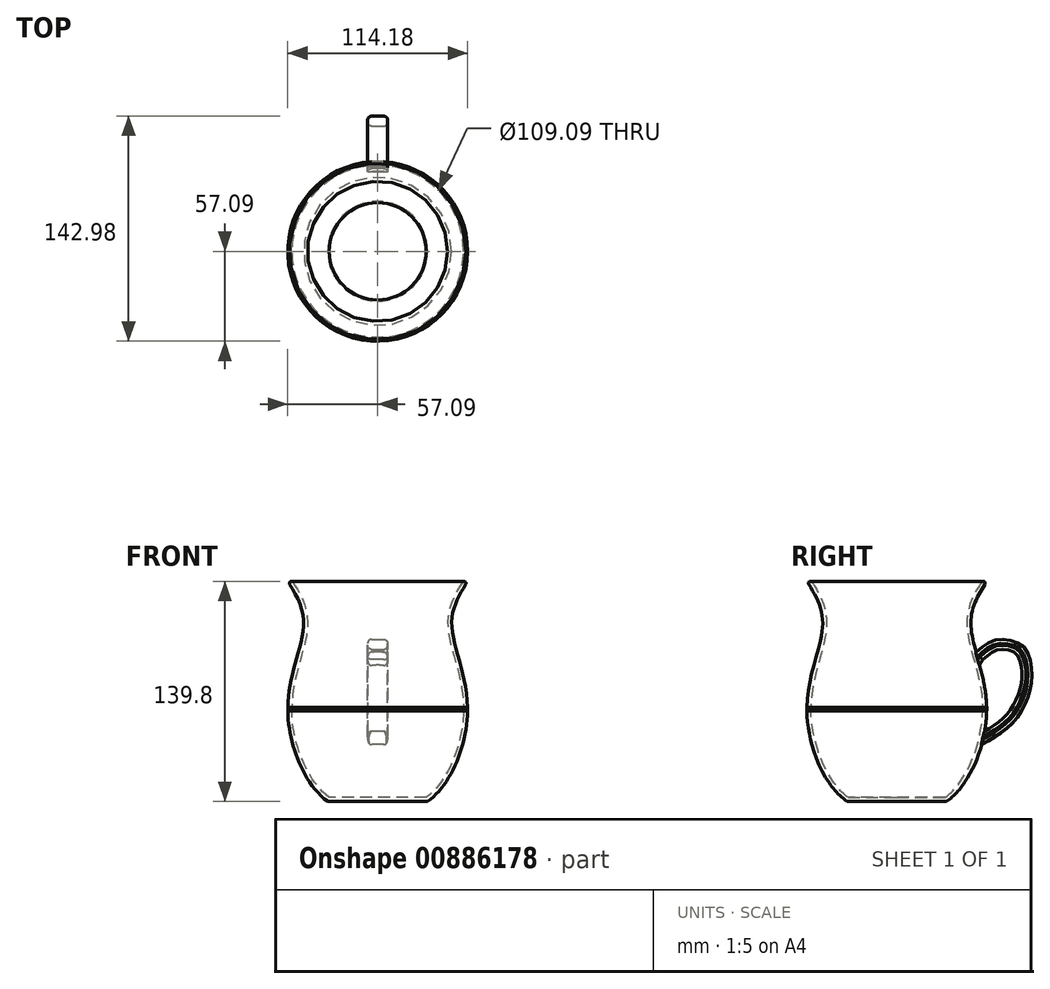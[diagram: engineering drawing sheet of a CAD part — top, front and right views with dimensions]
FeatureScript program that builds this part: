
annotation { "Feature Type Name" : "Feature", "Feature Type Description" : "" }
export const myFeature = defineFeature(function(context is Context, id is Id, definition is map)
    precondition{}
    {
        {
            var Q0;
            Q0=qCreatedBy(makeId("Front.planeOp"),FACE);
            var sketch = newSketch(context, id + "F0", { "sketchPlane" : qUnion([Q0])});
            skLineSegment(sketch, "E0.bottom", {"start": v(0, -69.9) * mm, "end": v(31.65, -69.9) * mm});
            skLineSegment(sketch, "E0.top", {"start": v(0, 69.9) * mm, "end": v(57.09, 69.9) * mm});
            skLineSegment(sketch, "E0.right", {"start": v(57.09, -12.27) * mm, "end": v(57.09, -10.35) * mm});
            skPoint(sketch, "E0.middle", {"position": v(0, 0) * mm});
            skFitSpline(sketch, "E1", {"points": [v(57.09, 69.9) * mm, v(47.03, 43.48) * mm, v(57.09, -10.35) * mm, v(31.65, -69.9) * mm, v(-8.28, -73.95) * mm], "startDerivative": vector(-76.93, -123.75) * mm, "endDerivative": vector(-181.25, 25.51) * mm});
            skLineSegment(sketch, "E2", {"start": v(0, 69.9) * mm, "end": v(0, -69.9) * mm});
            skPoint(sketch, "E3.orphan", {"position": v(57.09, -69.9) * mm});
            skPoint(sketch, "E0.left.end.orphan", {"position": v(-57.09, 69.9) * mm});
            skPoint(sketch, "E4.orphan", {"position": v(-57.09, -69.9) * mm});
            skSolve(sketch);
        }
        {
            var Q0;
            {var subQ3=sQuery(id+"F0.wireOp",EDGE,"E0.bottom");Q0=makeQuery(id+"F0.imprint","IMPRINT",FACE,{"disambiguationData":[TD([[makeQuery(id+"F0.imprint","IMPRINT",EDGE,{"derivedFrom":subQ3}),1.0]])]});}
            var Q1;
            Q1=sQuery(id+"F0.wireOp",EDGE,"E0.top");
            var Q2;
            Q2=sQuery(id+"F0.wireOp",EDGE,"E1");
            var Q3;
            Q3=sQuery(id+"F0.wireOp",EDGE,"E2");
            var Q4;
            Q4=sQuery(id+"F0.wireOp",EDGE,"E0.bottom");
            var Q5;
            Q5=sQuery(id+"F0.wireOp",EDGE,"E2");
            revolve(context, id + "F1", {"surfaceOperationType" : NewSurfaceOperationType.NEW, "entities" : qUnion([Q0]), "surfaceEntities" : qUnion([Q1, Q2, Q3, Q4]), "axis" : qUnion([Q5]), "revolveType" : RevolveType.FULL});
        }
        {
            var Q0;
            Q0=makeQuery(id+"F1.opRevolve","SWEPT_FACE",FACE,{"disambiguationData":[OSD([sQuery(id+"F0.wireOp",EDGE,"E0.top")])]});
            shell(context, id + "F2", {"entities" : qUnion([Q0]), "thickness" : 2.54 * mm});
        }
        {
            var Q0;
            Q0=qCreatedBy(makeId("Right.planeOp"),FACE);
            var sketch = newSketch(context, id + "F3", { "sketchPlane" : qUnion([Q0])});
            skFitSpline(sketch, "E5", {"points": [v(50.58, 25.14) * mm, v(63.89, 32.83) * mm, v(79.27, 29.28) * mm, v(84.3, 21.3) * mm, v(85.78, 7.7) * mm, v(80.75, -9.76) * mm, v(70.99, -22.48) * mm, v(52.95, -34.31) * mm], "startDerivative": vector(85.65, 71.96) * mm, "endDerivative": vector(-116.74, -67.27) * mm});
            skFitSpline(sketch, "E6.0", {"points": [v(54.66, 20.28) * mm, v(55.56, 21.03) * mm, v(57.26, 22.46) * mm, v(59.64, 24.26) * mm, v(61.47, 25.36) * mm, v(62.84, 25.99) * mm, v(63.68, 26.28) * mm, v(64.34, 26.45) * mm, v(64.75, 26.54) * mm, v(65.1, 26.6) * mm, v(65.44, 26.64) * mm, v(65.9, 26.69) * mm, v(66.5, 26.72) * mm, v(67.32, 26.72) * mm, v(68.4, 26.64) * mm, v(69.73, 26.45) * mm, v(71.5, 26.05) * mm, v(73.16, 25.47) * mm, v(74.53, 24.8) * mm, v(75.35, 24.3) * mm, v(75.92, 23.85) * mm, v(76.36, 23.42) * mm, v(76.73, 22.98) * mm, v(77.06, 22.46) * mm, v(77.4, 21.81) * mm, v(77.72, 21) * mm, v(78, 20.2) * mm, v(78.22, 19.45) * mm, v(78.44, 18.68) * mm, v(78.7, 17.68) * mm, v(79.05, 16.03) * mm, v(79.39, 13.85) * mm, v(79.54, 11.56) * mm, v(79.54, 9.68) * mm, v(79.48, 8.48) * mm, v(79.39, 7.5) * mm, v(79.28, 6.52) * mm, v(79.09, 5.25) * mm, v(78.79, 3.69) * mm, v(78.3, 1.58) * mm, v(77.52, -1.06) * mm, v(76.36, -4.17) * mm, v(75.02, -7.1) * mm, v(73.58, -9.74) * mm, v(72, -12.13) * mm, v(70.25, -14.34) * mm, v(68.25, -16.44) * mm, v(65.95, -18.48) * mm, v(63.23, -20.53) * mm, v(60.2, -22.6) * mm, v(56.9, -24.65) * mm, v(53.4, -26.72) * mm, v(51, -28.1) * mm, v(49.78, -28.8) * mm]});
            skFitSpline(sketch, "E7", {"points": [v(54.66, 20.28) * mm, v(51.17, 12.72) * mm, v(51.76, 11.54) * mm], "startDerivative": vector(-7.37, -12.87) * mm, "endDerivative": vector(3.07, -3.24) * mm});
            skLineSegment(sketch, "E8", {"start": v(50.58, 25.14) * mm, "end": v(48.03, 22.78) * mm});
            skLineSegment(sketch, "E9", {"start": v(49.96, 24.57) * mm, "end": v(52.2, 15.8) * mm});
            skLineSegment(sketch, "E10", {"start": v(55.67, -25.37) * mm, "end": v(53.65, -33.9) * mm});
            skSolve(sketch);
        }
        {
            var Q0;
            {var subQ3=sQuery(id+"F3.wireOp",EDGE,"E9");Q0=makeQuery(id+"F3.imprint","IMPRINT",FACE,{"disambiguationData":[TD([[makeQuery(id+"F3.imprint","IMPRINT",EDGE,{"derivedFrom":subQ3}),1.0]])]});}
            extrude(context, id + "F4", {"entities" : qUnion([Q0]), "operationType" : NewBodyOperationType.ADD, "depth" : 6.35 * mm, "offsetDistance" : 25.4 * mm, "hasSecondDirection" : true, "secondDirectionOppositeDirection" : true, "secondDirectionDepth" : 6.35 * mm});
        }
        {
            var Q0;
            Q0=makeQuery(id+"F4.opExtrude","CAP_EDGE",EDGE,{"disambiguationData":[OSD([sQuery(id+"F3.wireOp",EDGE,"E5")])],"isStart":false});
            var Q1;
            Q1=makeQuery(id+"F4.opExtrude","CAP_EDGE",EDGE,{"disambiguationData":[OSD([sQuery(id+"F3.wireOp",EDGE,"E5")])],"isStart":true});
            var Q2;
            Q2=makeQuery(id+"F4.opExtrude","CAP_EDGE",EDGE,{"disambiguationData":[OSD([sQuery(id+"F3.wireOp",EDGE,"E6.0")])],"isStart":true});
            var Q3;
            Q3=makeQuery(id+"F4.opExtrude","CAP_EDGE",EDGE,{"disambiguationData":[OSD([sQuery(id+"F3.wireOp",EDGE,"E7")])],"isStart":true});
            var Q4;
            Q4=makeQuery(id+"F4.opExtrude","CAP_EDGE",EDGE,{"disambiguationData":[OSD([sQuery(id+"F3.wireOp",EDGE,"E6.0")])],"isStart":false});
            var Q5;
            Q5=makeQuery(id+"F4.opExtrude","CAP_EDGE",EDGE,{"disambiguationData":[OSD([sQuery(id+"F3.wireOp",EDGE,"E7")])],"isStart":false});
            fillet(context, id + "F5", {"entities" : qUnion([Q0, Q1, Q2, Q3, Q4, Q5]), "radius" : 2.54 * mm, "tangentPropagation" : true, "allowEdgeOverflow" : false});
        }
        {
            var Q0;
            Q0=makeQuery(id+"F2.opShell","OFFSET_EDGE",EDGE,{"disambiguationData":[OSD([sQuery(id+"F0.wireOp",EDGE,"E0.top"),sQuery(id+"F0.wireOp",EDGE,"E1")])]});
            var Q1;
            Q1=makeQuery(id+"F1.opRevolve","SWEPT_EDGE",EDGE,{"disambiguationData":[OSD([sQuery(id+"F0.wireOp",EDGE,"E0.top"),sQuery(id+"F0.wireOp",EDGE,"E1")])]});
            fillet(context, id + "F6", {"entities" : qUnion([Q0, Q1]), "radius" : 1.27 * mm, "tangentPropagation" : true, "allowEdgeOverflow" : false});
        }
    });
